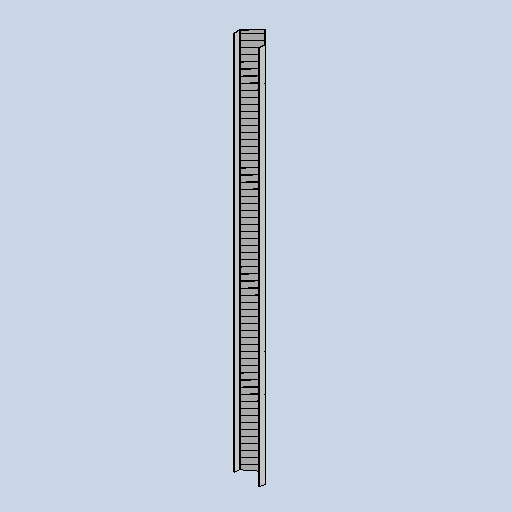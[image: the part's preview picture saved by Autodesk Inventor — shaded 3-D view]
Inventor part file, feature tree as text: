
AUTODESK INVENTOR PART (.ipt)
format: ipt  version: 2025 (Build 290162010, 162A)  size: 1,314,816 bytes
history: native  units: mm
features: projected_geometry x7, sketch x4, sheet_metal_op x3, other x3, mirror x1, extrude x1
ambient origin geometry x8: Origin, YZ Plane, XZ Plane, XY Plane, X Axis, Y Axis, Z Axis, Center Point
bodies: Body1 (feature_tree)
feature tree (19):
  sheet_metal_op  "Contour Flange1"
  mirror  "Mirror2"
  extrude  "Extrusion4"  Depth=1.0mm
  sketch  "Sketch3"  dims[d15=10.0mm d18=1.0mm]
  other  "Plate1"
  sheet_metal_op  "Bend1"
  sheet_metal_op  "Corner1"
  sketch  "Sketch5"  dims[d20=1.0mm]
  sketch  "Sketch Rectangular Pattern3"  dims[d19=1.0mm]
  sketch  "Sketch9"  dims[d21=0.8mm d22=0.8mm d23=0.4mm d24=1.6mm d25=0.8mm d26=625.0mm d27=0.8mm d28=0.8mm d29=3.2mm d30=0.8mm d31=0.8mm d32=42.0mm d33=15.358897mm d111=0.2mm d112=28.0mm d113=5.0mm d114=0.5mm d115=620.0mm d116=10.0mm d73=10.0mm d75=10.0mm d97=5.0mm d98=0.8mm d99=0.0mm d100=1.396263mm d101=0.0mm d102=0.0mm d103=0.5mm d104=0.872665mm]
  projected_geometry  "Projected Loop4"
  projected_geometry  "Projected Loop5"
  projected_geometry  "Projected Loop6"
  projected_geometry  "Projected Loop7"
  projected_geometry  "Projected Loop8"
  projected_geometry  "Projected Loop9"
  projected_geometry  "Projected Loop10"
  other  "Cut3"
  other  "Definition1"
